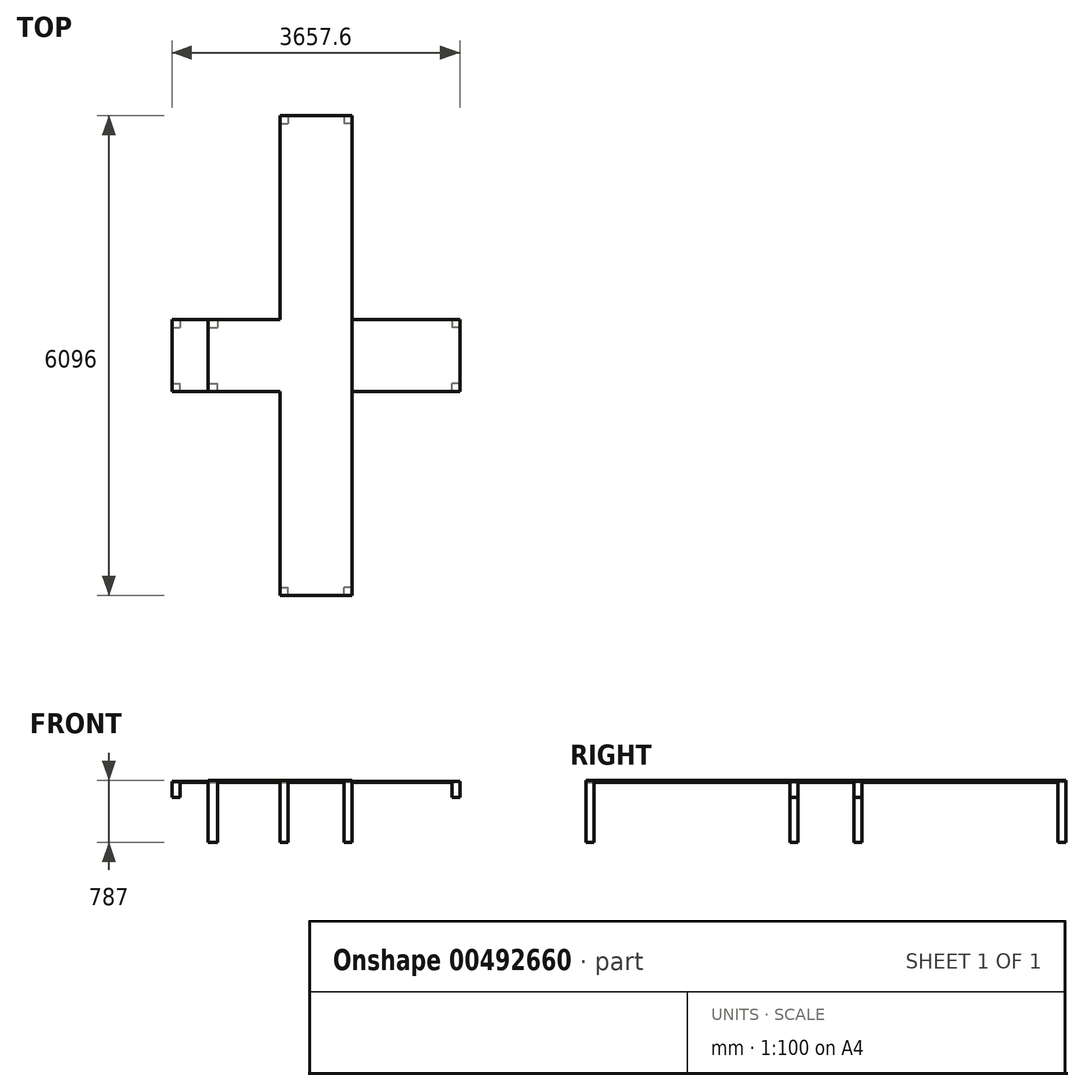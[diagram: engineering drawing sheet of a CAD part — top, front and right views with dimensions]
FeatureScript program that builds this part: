
annotation { "Feature Type Name" : "Feature", "Feature Type Description" : "" }
export const myFeature = defineFeature(function(context is Context, id is Id, definition is map)
    precondition{}
    {
        {
            var Q0;
            Q0=qCreatedBy(makeId("Top.planeOp"),FACE);
            var sketch = newSketch(context, id + "F0", { "sketchPlane" : qUnion([Q0])});
            skLineSegment(sketch, "E0.bottom", {"start": v(1828.8, -457.2) * mm, "end": v(-1828.8, -457.2) * mm});
            skLineSegment(sketch, "E0.top", {"start": v(1828.8, 457.2) * mm, "end": v(-1828.8, 457.2) * mm});
            skLineSegment(sketch, "E0.left", {"start": v(1828.8, -457.2) * mm, "end": v(1828.8, 457.2) * mm});
            skLineSegment(sketch, "E0.right", {"start": v(-1828.8, -457.2) * mm, "end": v(-1828.8, 457.2) * mm});
            skPoint(sketch, "E0.middle", {"position": v(0, 0) * mm});
            skSolve(sketch);
        }
        {
            var Q0;
            Q0 = qSketchRegion(id + "F0", true);
            extrude(context, id + "F1", {"entities" : qUnion([Q0]), "depth" : 12.7 * mm, "offsetDistance" : 25 * mm});
        }
        {
            var Q0;
            Q0=makeQuery(id+"F1.opExtrude","CAP_FACE",FACE,{"disambiguationData":[OSD([sQuery(id+"F0.wireOp",EDGE,"E0.bottom"),sQuery(id+"F0.wireOp",EDGE,"E0.top"),sQuery(id+"F0.wireOp",EDGE,"E0.left"),sQuery(id+"F0.wireOp",EDGE,"E0.right")])],"isStart":true});
            var sketch = newSketch(context, id + "F2", { "sketchPlane" : qUnion([Q0])});
            skLineSegment(sketch, "E1", {"start": v(0, 457.2) * mm, "end": v(0, -457.2) * mm, "construction": true});
            skLineSegment(sketch, "E2", {"start": v(-1828.8, 0) * mm, "end": v(1828.8, 0) * mm, "construction": true});
            skLineSegment(sketch, "E3.bottom", {"start": v(-1828.8, 457.2) * mm, "end": v(-1727.2, 457.2) * mm});
            skLineSegment(sketch, "E3.top", {"start": v(-1828.8, 355.6) * mm, "end": v(-1727.2, 355.6) * mm});
            skLineSegment(sketch, "E3.left", {"start": v(-1828.8, 457.2) * mm, "end": v(-1828.8, 355.6) * mm});
            skLineSegment(sketch, "E3.right", {"start": v(-1727.2, 457.2) * mm, "end": v(-1727.2, 355.6) * mm});
            skLineSegment(sketch, "E4.MirrorCS", {"start": v(1727.2, 457.2) * mm, "end": v(1727.2, 355.6) * mm});
            skLineSegment(sketch, "E5.MirrorCS", {"start": v(1828.8, 457.2) * mm, "end": v(1727.2, 457.2) * mm});
            skLineSegment(sketch, "E6.MirrorCS", {"start": v(1828.8, 457.2) * mm, "end": v(1828.8, 355.6) * mm});
            skLineSegment(sketch, "E7.MirrorCS", {"start": v(1828.8, 355.6) * mm, "end": v(1727.2, 355.6) * mm});
            skLineSegment(sketch, "E8.MirrorCS", {"start": v(-1828.8, -355.6) * mm, "end": v(-1727.2, -355.6) * mm});
            skLineSegment(sketch, "E9.MirrorCS", {"start": v(-1727.2, -457.2) * mm, "end": v(-1727.2, -355.6) * mm});
            skLineSegment(sketch, "E10.MirrorCS", {"start": v(-1828.8, -457.2) * mm, "end": v(-1727.2, -457.2) * mm});
            skLineSegment(sketch, "E11.MirrorCS", {"start": v(-1828.8, -457.2) * mm, "end": v(-1828.8, -355.6) * mm});
            skLineSegment(sketch, "E12.MirrorCS", {"start": v(1727.2, -457.2) * mm, "end": v(1727.2, -355.6) * mm});
            skLineSegment(sketch, "E13.MirrorCS", {"start": v(1828.8, -355.6) * mm, "end": v(1727.2, -355.6) * mm});
            skLineSegment(sketch, "E14.MirrorCS", {"start": v(1828.8, -457.2) * mm, "end": v(1828.8, -355.6) * mm});
            skLineSegment(sketch, "E15.MirrorCS", {"start": v(1828.8, -457.2) * mm, "end": v(1727.2, -457.2) * mm});
            skSolve(sketch);
        }
        {
            var Q0;
            Q0 = qSketchRegion(id + "F2", true);
            extrude(context, id + "F3", {"entities" : qUnion([Q0]), "operationType" : NewBodyOperationType.ADD, "depth" : 190.5 * mm, "offsetDistance" : 25 * mm});
        }
        {
            var Q0;
            Q0=qCreatedBy(makeId("Top.planeOp"),FACE);
            var sketch = newSketch(context, id + "F4", { "sketchPlane" : qUnion([Q0])});
            skLineSegment(sketch, "E16.bottom", {"start": v(457.2, -3048) * mm, "end": v(-457.2, -3048) * mm});
            skLineSegment(sketch, "E16.top", {"start": v(457.2, 3048) * mm, "end": v(-457.2, 3048) * mm});
            skLineSegment(sketch, "E16.left", {"start": v(457.2, -3048) * mm, "end": v(457.2, 3048) * mm});
            skLineSegment(sketch, "E16.right", {"start": v(-457.2, -3048) * mm, "end": v(-457.2, 3048) * mm});
            skPoint(sketch, "E16.middle", {"position": v(0, 0) * mm});
            skLineSegment(sketch, "E17.bottom", {"start": v(-457.2, -457.2) * mm, "end": v(-1371.6, -457.2) * mm});
            skLineSegment(sketch, "E17.top", {"start": v(-457.2, 457.2) * mm, "end": v(-1371.6, 457.2) * mm});
            skLineSegment(sketch, "E17.left", {"start": v(-457.2, -457.2) * mm, "end": v(-457.2, 457.2) * mm});
            skLineSegment(sketch, "E17.right", {"start": v(-1371.6, -457.2) * mm, "end": v(-1371.6, 457.2) * mm});
            skPoint(sketch, "E17.middle", {"position": v(-914.4, 0) * mm});
            skSolve(sketch);
        }
        {
            var Q0;
            Q0 = qSketchRegion(id + "F4", true);
            extrude(context, id + "F5", {"entities" : qUnion([Q0]), "depth" : 25 * mm, "offsetDistance" : 25 * mm});
        }
        {
            var Q0;
            Q0=makeQuery(id+"F5.opExtrude","CAP_FACE",FACE,{"disambiguationData":[OSD([sQuery(id+"F4.wireOp",EDGE,"E16.bottom"),sQuery(id+"F4.wireOp",EDGE,"E16.top"),sQuery(id+"F4.wireOp",EDGE,"E16.left"),sQuery(id+"F4.wireOp",EDGE,"E16.right"),sQuery(id+"F4.wireOp",EDGE,"E17.bottom"),sQuery(id+"F4.wireOp",EDGE,"E17.top"),sQuery(id+"F4.wireOp",EDGE,"E17.right")])],"isStart":true});
            var sketch = newSketch(context, id + "F6", { "sketchPlane" : qUnion([Q0])});
            skLineSegment(sketch, "E18.bottom", {"start": v(-457.2, 3048) * mm, "end": v(-355.6, 3048) * mm});
            skLineSegment(sketch, "E18.top", {"start": v(-457.2, 2946.4) * mm, "end": v(-355.6, 2946.4) * mm});
            skLineSegment(sketch, "E18.left", {"start": v(-457.2, 3048) * mm, "end": v(-457.2, 2946.4) * mm});
            skLineSegment(sketch, "E18.right", {"start": v(-355.6, 3048) * mm, "end": v(-355.6, 2946.4) * mm});
            skLineSegment(sketch, "E19", {"start": v(0, 3048) * mm, "end": v(0, 2740.91) * mm, "construction": true});
            skPoint(sketch, "E19.endSnap0", {"position": v(0, 3048) * mm});
            skLineSegment(sketch, "E20", {"start": v(-1371.6, 0) * mm, "end": v(457.2, 0) * mm, "construction": true});
            skLineSegment(sketch, "E21.MirrorCS", {"start": v(457.2, 2946.4) * mm, "end": v(355.6, 2946.4) * mm});
            skLineSegment(sketch, "E22.MirrorCS", {"start": v(355.6, 3048) * mm, "end": v(355.6, 2946.4) * mm});
            skLineSegment(sketch, "E23.MirrorCS", {"start": v(457.2, 3048) * mm, "end": v(355.6, 3048) * mm});
            skLineSegment(sketch, "E24.MirrorCS", {"start": v(457.2, 3048) * mm, "end": v(457.2, 2946.4) * mm});
            skLineSegment(sketch, "E25.MirrorCS", {"start": v(-457.2, -2946.4) * mm, "end": v(-355.6, -2946.4) * mm});
            skLineSegment(sketch, "E26.MirrorCS", {"start": v(-355.6, -3048) * mm, "end": v(-355.6, -2946.4) * mm});
            skLineSegment(sketch, "E27.MirrorCS", {"start": v(-457.2, -3048) * mm, "end": v(-355.6, -3048) * mm});
            skLineSegment(sketch, "E28.MirrorCS", {"start": v(-457.2, -3048) * mm, "end": v(-457.2, -2946.4) * mm});
            skLineSegment(sketch, "E29.MirrorCS", {"start": v(355.6, -3048) * mm, "end": v(355.6, -2946.4) * mm});
            skLineSegment(sketch, "E30.MirrorCS", {"start": v(457.2, -2946.4) * mm, "end": v(355.6, -2946.4) * mm});
            skLineSegment(sketch, "E31.MirrorCS", {"start": v(457.2, -3048) * mm, "end": v(355.6, -3048) * mm});
            skLineSegment(sketch, "E32.MirrorCS", {"start": v(457.2, -3048) * mm, "end": v(457.2, -2946.4) * mm});
            skLineSegment(sketch, "E33.bottom", {"start": v(-1371.6, 457.2) * mm, "end": v(-1246.2, 457.2) * mm});
            skLineSegment(sketch, "E33.top", {"start": v(-1371.6, 355.6) * mm, "end": v(-1246.2, 355.6) * mm});
            skLineSegment(sketch, "E33.left", {"start": v(-1371.6, 457.2) * mm, "end": v(-1371.6, 355.6) * mm});
            skLineSegment(sketch, "E33.right", {"start": v(-1246.2, 457.2) * mm, "end": v(-1246.2, 355.6) * mm});
            skLineSegment(sketch, "E34.MirrorCS", {"start": v(-1371.6, -355.6) * mm, "end": v(-1246.2, -355.6) * mm});
            skLineSegment(sketch, "E35.MirrorCS", {"start": v(-1371.6, -457.2) * mm, "end": v(-1371.6, -355.6) * mm});
            skLineSegment(sketch, "E36.MirrorCS", {"start": v(-1371.6, -457.2) * mm, "end": v(-1246.2, -457.2) * mm});
            skLineSegment(sketch, "E37.MirrorCS", {"start": v(-1246.2, -457.2) * mm, "end": v(-1246.2, -355.6) * mm});
            skSolve(sketch);
        }
        {
            var Q0;
            Q0 = qSketchRegion(id + "F6", true);
            extrude(context, id + "F7", {"entities" : qUnion([Q0]), "operationType" : NewBodyOperationType.ADD, "depth" : 762 * mm, "offsetDistance" : 25 * mm});
        }
    });
